# Revit family: Zaniboni-Bongo-3_Inch_Fully_Adj_Surface_Mounted-1
name_source: partatom
category: Lighting Fixtures
revit_build: Autodesk Revit 2016 (Build: 20150220_1215(x64)
units: mm (PartAtom-declared; Revit-internal decimal feet)

## family parameters
Cut with Voids When Loaded = No
Host = Face
Light Source = Yes
Part Type = Normal
Room Calculation Point = No
Round Connector Dimension = Use Diameter
Shared = No

## types (2) — shared parameters
Assembly Code = E1020300
Base Finish = ZBN - Metal Matte White
Beam = 24°
Body Finish = ZBN - Metal Matte White
CRI = 80
Color Filter = 16777215
Default Elevation = 48"
Diameter = 4"
Diffuser Finish = ZBN - Metal Matte White
Dimming Lamp Color Temperature Shift = <None>
Emit Shape Visible in Rendering = No
Emit from Circle Diameter = 24"
Front Finish = ZBN - Metal Matte Black
Integrated Finish = ZBN - Metal Matte White
Kelvin = 2700K
Keynote = 12500
Manufacturer = Zaniboni
Mechanism Finish = ZBN - Metal Matte Black
Photometric Web File = generic
Screen Finish = ZBN - Glass
Support Finish = ZBN - Metal Matte White
Tilt Angle = 90.00°
Type Comments = Bongo
URL = www.zanibonilighting.com
Voltage = 120 V
Wattage Comments = 9W

## per-type parameters (varying)
| type | Description | Height | Height L | Integrated |
| S3-BON3J-0927A-2C-WS-Remote | 3 Inch light source Round Fully Adjustable Surface Mounted Monopoint | 5 1/2" | 5 1/8" | No |
| S3-BON3J-0927A-2C-WS-Integrated | 3 Inch light source Round Fully Adjustable Surface Mounted Monopoint Integrated | 8 5/8" | 8 1/8" | Yes |

note: column(s) folded — value = type name in every type: Model

## geometry (parser evidence)
native form markers: Sweep x6
no freeform markers — native parametric forms only
